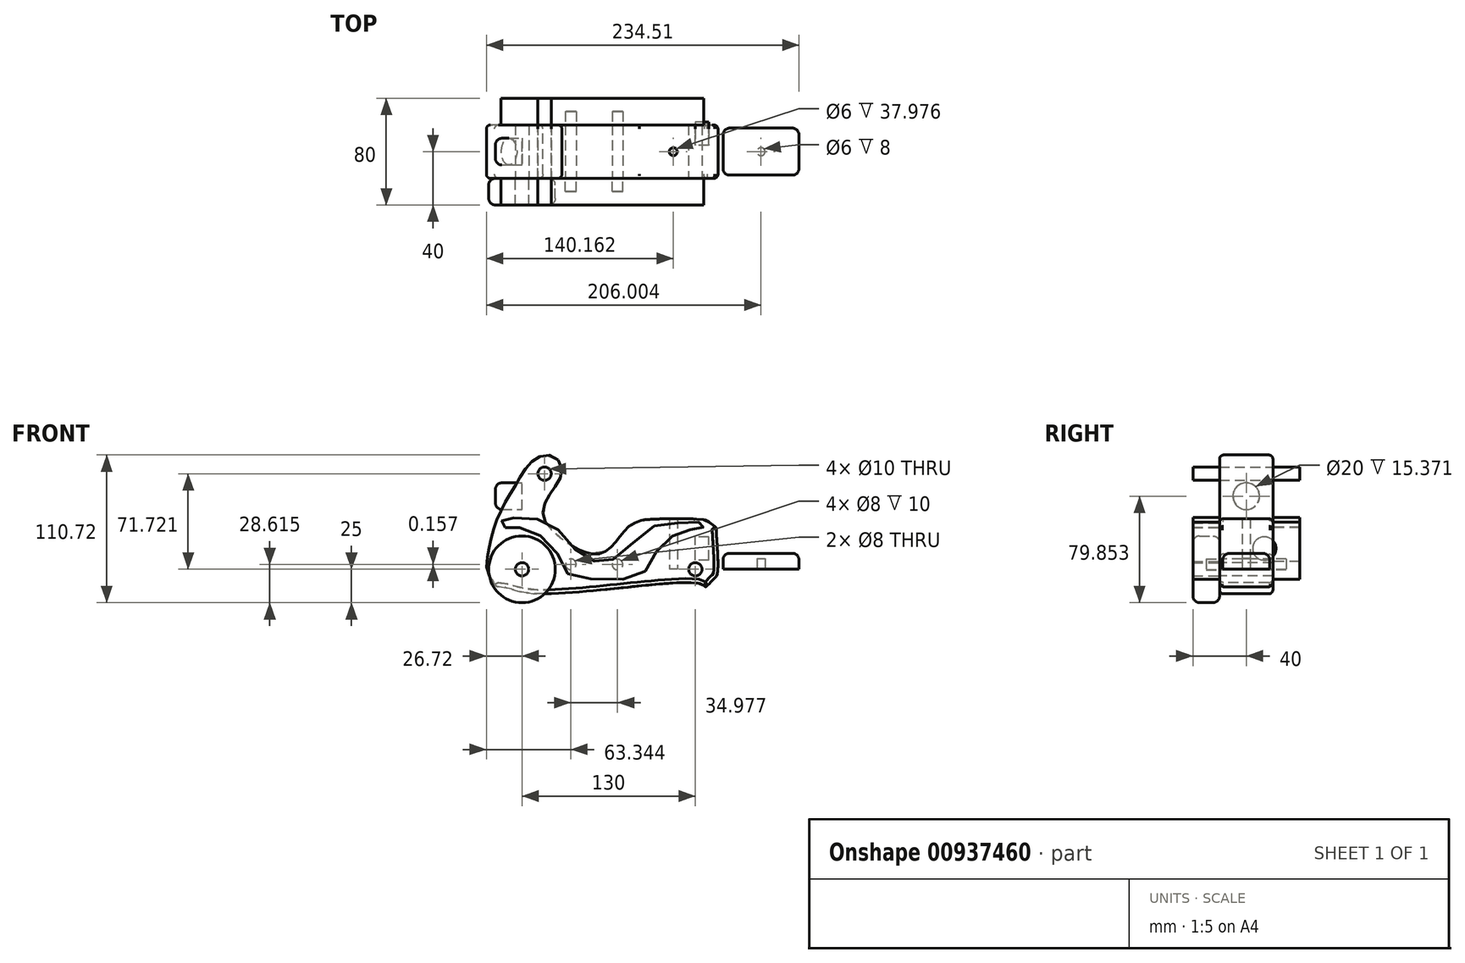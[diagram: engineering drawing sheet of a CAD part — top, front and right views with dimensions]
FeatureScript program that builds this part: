
annotation { "Feature Type Name" : "Feature", "Feature Type Description" : "" }
export const myFeature = defineFeature(function(context is Context, id is Id, definition is map)
    precondition{}
    {
        {
            var Q0;
            Q0=qCreatedBy(makeId("Front.planeOp"),FACE);
            var sketch = newSketch(context, id + "F0", { "sketchPlane" : qUnion([Q0])});
            skCircle(sketch, "E0", {"center": v(0, 0) * mm, "radius": 25 * mm});
            skCircle(sketch, "E1", {"center": v(-130, 0) * mm, "radius": 25 * mm});
            skFitSpline(sketch, "E2", {"points": [v(-142.69, -13.62) * mm, v(3.6, -12.42) * mm, v(8.41, -12.12) * mm, v(12.62, -8.21) * mm, v(15.19, -2.69) * mm, v(15.43, 27.55) * mm, v(14.22, 32.15) * mm, v(11.32, 34.57) * mm, v(6.48, 36.02) * mm, v(-39.96, 36.5) * mm, v(-42.38, 36.02) * mm, v(-48.19, 32.39) * mm, v(-69, 16.67) * mm, v(-87.38, 16.67) * mm, v(-103.82, 27.55) * mm, v(-111.42, 41.65) * mm, v(-106.78, 59.25) * mm, v(-102.15, 74.08) * mm, v(-106.78, 82.42) * mm, v(-117.9, 81.5) * mm, v(-132.73, 65.28) * mm, v(-147.55, 37.02) * mm, v(-154.96, 10.15) * mm, v(-154.9, -3) * mm, v(-152.19, -8.1) * mm, v(-142.69, -13.62) * mm]});
            skSolve(sketch);
        }
        {
            var Q0;
            Q0=qCreatedBy(makeId("Front.planeOp"),FACE);
            var sketch = newSketch(context, id + "F1", { "sketchPlane" : qUnion([Q0])});
            skFitSpline(sketch, "E3.0", {"points": [v(-142.69, -13.62) * mm, v(-117.23, -18.37) * mm, v(4.2, -10.93) * mm, v(7.9, -13.06) * mm, v(13.19, -7.76) * mm, v(16.42, -3.45) * mm, v(15.75, 27.66) * mm, v(14.86, 32.04) * mm, v(10.84, 34.95) * mm, v(7.36, 36.95) * mm, v(-40.36, 36.86) * mm, v(-42.2, 36.14) * mm, v(-49.45, 32.5) * mm, v(-68.05, 13.1) * mm, v(-87.85, 15.1) * mm, v(-104.52, 26.51) * mm, v(-114.25, 41.4) * mm, v(-107.03, 59.23) * mm, v(-100.08, 73.44) * mm, v(-105.87, 84.46) * mm, v(-119.96, 82.96) * mm, v(-133.88, 64.85) * mm, v(-148.53, 37.95) * mm, v(-155.6, 11.4) * mm, v(-155.9, -2.85) * mm, v(-151.67, -8.64) * mm, v(-149.66, -12.32) * mm, v(-142.69, -13.62) * mm]});
            skSolve(sketch);
        }
        {
            var Q0;
            Q0 = qSketchRegion(id + "F1", true);
            extrude(context, id + "F2", {"entities" : qUnion([Q0]), "depth" : 20 * mm, "offsetDistance" : 25 * mm, "hasSecondDirection" : true, "secondDirectionOppositeDirection" : true, "secondDirectionDepth" : 20 * mm});
        }
        {
            var Q0;
            Q0=makeQuery(id+"F2.opExtrude","CAP_FACE",FACE,{"disambiguationData":[OSD([sQuery(id+"F1.wireOp",EDGE,"E3.0")])],"isStart":false});
            var sketch = newSketch(context, id + "F3", { "sketchPlane" : qUnion([Q0])});
            skCircle(sketch, "E4", {"center": v(-113.08, 71.72) * mm, "radius": 5 * mm});
            skCircle(sketch, "E5", {"center": v(-130, 0) * mm, "radius": 5 * mm});
            skCircle(sketch, "E6", {"center": v(0, 0) * mm, "radius": 5 * mm});
            skCircle(sketch, "E7", {"center": v(-93.38, 3.77) * mm, "radius": 4 * mm});
            skCircle(sketch, "E8", {"center": v(-58.4, 3.61) * mm, "radius": 4 * mm});
            skSolve(sketch);
        }
        {
            var Q0;
            Q0 = qSketchRegion(id + "F3", true);
            extrude(context, id + "F4", {"entities" : qUnion([Q0]), "operationType" : NewBodyOperationType.REMOVE, "endBound" : BoundingType.THROUGH_ALL, "oppositeDirection" : true, "depth" : 25 * mm, "offsetDistance" : 25 * mm});
        }
        {
            var Q0;
            Q0=makeQuery(id+"F2.opExtrude","CAP_EDGE",EDGE,{"disambiguationData":[OSD([sQuery(id+"F1.wireOp",EDGE,"E3.0")])],"isStart":false});
            var Q1;
            Q1=makeQuery(id+"F2.opExtrude","CAP_EDGE",EDGE,{"disambiguationData":[OSD([sQuery(id+"F1.wireOp",EDGE,"E3.0")])],"isStart":true});
            fillet(context, id + "F5", {"entities" : qUnion([Q0, Q1]), "radius" : 3 * mm, "tangentPropagation" : true, "allowEdgeOverflow" : false});
        }
        {
            var Q0;
            Q0=makeQuery(id+"F2.opExtrude","CAP_FACE",FACE,{"disambiguationData":[OSD([sQuery(id+"F1.wireOp",EDGE,"E3.0")])],"isStart":false});
            var sketch = newSketch(context, id + "F6", { "sketchPlane" : qUnion([Q0])});
            skFitSpline(sketch, "E9", {"points": [v(-142.57, 31.36) * mm, v(-136.56, 31.66) * mm, v(-122.6, 28.43) * mm, v(-105.17, 15) * mm, v(-95.7, -3.19) * mm, v(-74.3, -7.15) * mm, v(-41.33, -4.69) * mm, v(-32.02, 8.83) * mm, v(-18.8, 23.85) * mm, v(-6.49, 29.25) * mm, v(4.03, 30.46) * mm, v(6.11, 31.78) * mm, v(6.11, 34.02) * mm, v(3.37, 35.44) * mm, v(-10.73, 34.74) * mm, v(-32.01, 31.84) * mm, v(-56.2, 11.04) * mm, v(-65.88, 6.44) * mm, v(-81.93, 8.1) * mm, v(-98.45, 25.17) * mm, v(-115.7, 36.78) * mm, v(-136.43, 38.66) * mm, v(-144.17, 37.2) * mm, v(-145.3, 35.8) * mm, v(-145.64, 32.92) * mm, v(-142.57, 31.36) * mm]});
            skSolve(sketch);
        }
        {
            var Q0;
            Q0 = qSketchRegion(id + "F6", true);
            extrude(context, id + "F7", {"entities" : qUnion([Q0]), "depth" : 20 * mm, "offsetDistance" : 25 * mm});
        }
        {
            var Q0;
            Q0=makeQuery(id+"F7.opExtrude","CAP_FACE",FACE,{"disambiguationData":[OSD([sQuery(id+"F6.wireOp",EDGE,"E9")])],"isStart":true});
            var sketch = newSketch(context, id + "F8", { "sketchPlane" : qUnion([Q0])});
            skCircle(sketch, "E10.0", {"center": v(58.4, 3.61) * mm, "radius": 4 * mm});
            skCircle(sketch, "E11.0", {"center": v(93.38, 3.77) * mm, "radius": 4 * mm});
            skSolve(sketch);
        }
        {
            var Q0;
            Q0 = qSketchRegion(id + "F8", true);
            extrude(context, id + "F9", {"entities" : qUnion([Q0]), "operationType" : NewBodyOperationType.REMOVE, "oppositeDirection" : true, "depth" : 10 * mm, "offsetDistance" : 25 * mm});
        }
        {
            var Q0;
            Q0=qCreatedBy(makeId("Front.planeOp"),FACE);
            var sketch = newSketch(context, id + "F10", { "sketchPlane" : qUnion([Q0])});
            skCircle(sketch, "E12.0", {"center": v(-113.08, 71.72) * mm, "radius": 5 * mm});
            skSolve(sketch);
        }
        {
            var Q0;
            Q0 = qSketchRegion(id + "F10", true);
            extrude(context, id + "F11", {"entities" : qUnion([Q0]), "depth" : 40 * mm, "offsetDistance" : 25 * mm, "hasSecondDirection" : true, "secondDirectionOppositeDirection" : true, "secondDirectionDepth" : 40 * mm});
        }
        {
            var Q0;
            Q0=makeQuery(id+"F2.opExtrude","CAP_FACE",FACE,{"disambiguationData":[OSD([sQuery(id+"F1.wireOp",EDGE,"E3.0")])],"isStart":false});
            var sketch = newSketch(context, id + "F12", { "sketchPlane" : qUnion([Q0])});
            skCircle(sketch, "E13.0", {"center": v(-130, 0) * mm, "radius": 25 * mm});
            skCircle(sketch, "E14.0", {"center": v(-130, 0) * mm, "radius": 5 * mm});
            skSolve(sketch);
        }
        {
            var Q0;
            Q0 = qSketchRegion(id + "F12", true);
            extrude(context, id + "F13", {"entities" : qUnion([Q0]), "depth" : 20 * mm, "offsetDistance" : 25 * mm});
        }
        {
            var Q0;
            Q0=makeQuery(id+"F13.opExtrude","CAP_EDGE",EDGE,{"disambiguationData":[OSD([sQuery(id+"F12.wireOp",EDGE,"E13.0")])],"isStart":false});
            var Q1;
            {var subQ0=sQuery(id+"F12.wireOp",EDGE,"E13.0");Q1=makeQuery(id+"F13.boolean.opBoolean","SPLIT",EDGE,{"disambiguationData":[topologyDisambiguationEdgeConnected([makeQuery(id+"F13.opExtrude","CAP_FACE",FACE,{"disambiguationData":[OSD([subQ0,sQuery(id+"F12.wireOp",EDGE,"E14.0")])],"isStart":true})])],"derivedFrom":makeQuery(id+"F13.opExtrude","CAP_EDGE",EDGE,{"disambiguationData":[OSD([subQ0])],"isStart":true})});}
            fillet(context, id + "F14", {"entities" : qUnion([Q0, Q1]), "radius" : 5 * mm, "tangentPropagation" : true, "allowEdgeOverflow" : false});
        }
        {
            var Q0;
            Q0=makeQuery(id+"F7.opExtrude","SWEPT_BODY",BODY,{"disambiguationData":[OSD([sQuery(id+"F6.wireOp",EDGE,"E9")])]});
            var Q1;
            Q1=qCreatedBy(makeId("Front.planeOp"),FACE);
            mirror(context, id + "F15", {"entities" : qUnion([Q0]), "mirrorPlane" : qUnion([Q1])});
        }
        {
            var Q0;
            Q0=qCreatedBy(makeId("Right.planeOp"),FACE);
            cPlane(context, id + "F16", {"entities" : qUnion([Q0]), "cplaneType" : CPlaneType.OFFSET, "offset" : 130 * mm, "oppositeDirection" : true, "width" : 150 * mm, "height" : 150 * mm});
        }
        {
            var Q0;
            Q0=qCreatedBy(id+"F16.planeOp",FACE);
            var sketch = newSketch(context, id + "F17", { "sketchPlane" : qUnion([Q0])});
            skCircle(sketch, "E15", {"center": v(0, 54.85) * mm, "radius": 10 * mm});
            skSolve(sketch);
        }
        {
            var Q0;
            Q0 = qSketchRegion(id + "F17", true);
            extrude(context, id + "F18", {"entities" : qUnion([Q0]), "operationType" : NewBodyOperationType.REMOVE, "oppositeDirection" : true, "depth" : 20 * mm, "offsetDistance" : 25 * mm});
        }
        {
            var Q0;
            Q0=makeQuery(id+"F18.boolean.opBoolean","COPY",FACE,{"derivedFrom":makeQuery(id+"F18.opExtrude","CAP_FACE",FACE,{"disambiguationData":[OSD([sQuery(id+"F17.wireOp",EDGE,"E15")])],"isStart":true})});
            var sketch = newSketch(context, id + "F19", { "sketchPlane" : qUnion([Q0])});
            skCircle(sketch, "E16.0", {"center": v(0, 54.85) * mm, "radius": 10 * mm});
            skSolve(sketch);
        }
        {
            var Q0;
            Q0 = qSketchRegion(id + "F19", true);
            extrude(context, id + "F20", {"entities" : qUnion([Q0]), "depth" : 20 * mm, "offsetDistance" : 25 * mm});
        }
        {
            var Q0;
            Q0=makeQuery(id+"F20.opExtrude","CAP_EDGE",EDGE,{"disambiguationData":[OSD([sQuery(id+"F19.wireOp",EDGE,"E16.0")])],"isStart":false});
            fillet(context, id + "F21", {"entities" : qUnion([Q0]), "radius" : 5 * mm, "tangentPropagation" : true, "allowEdgeOverflow" : false});
        }
        {
            var Q0;
            Q0=qCreatedBy(makeId("Top.planeOp"),FACE);
            var sketch = newSketch(context, id + "F22", { "sketchPlane" : qUnion([Q0])});
            skLineSegment(sketch, "E17.bottom", {"start": v(77.8, 17.62) * mm, "end": v(20.78, 17.62) * mm});
            skLineSegment(sketch, "E17.top", {"start": v(77.8, -17.62) * mm, "end": v(20.78, -17.62) * mm});
            skLineSegment(sketch, "E17.left", {"start": v(77.8, 17.62) * mm, "end": v(77.8, -17.62) * mm});
            skLineSegment(sketch, "E17.right", {"start": v(20.78, 17.62) * mm, "end": v(20.78, -17.62) * mm});
            skPoint(sketch, "E17.middle", {"position": v(49.28, 0) * mm});
            skSolve(sketch);
        }
        {
            var Q0;
            Q0 = qSketchRegion(id + "F22", true);
            extrude(context, id + "F23", {"entities" : qUnion([Q0]), "depth" : 12 * mm, "offsetDistance" : 25 * mm});
        }
        {
            var Q0;
            Q0=makeQuery(id+"F23.opExtrude","SWEPT_EDGE",EDGE,{"disambiguationData":[OSD([sQuery(id+"F22.wireOp",EDGE,"E17.bottom"),sQuery(id+"F22.wireOp",EDGE,"E17.left")])]});
            var Q1;
            Q1=makeQuery(id+"F23.opExtrude","SWEPT_EDGE",EDGE,{"disambiguationData":[OSD([sQuery(id+"F22.wireOp",EDGE,"E17.top"),sQuery(id+"F22.wireOp",EDGE,"E17.left")])]});
            var Q2;
            Q2=makeQuery(id+"F23.opExtrude","SWEPT_EDGE",EDGE,{"disambiguationData":[OSD([sQuery(id+"F22.wireOp",EDGE,"E17.top"),sQuery(id+"F22.wireOp",EDGE,"E17.right")])]});
            var Q3;
            Q3=makeQuery(id+"F23.opExtrude","SWEPT_EDGE",EDGE,{"disambiguationData":[OSD([sQuery(id+"F22.wireOp",EDGE,"E17.bottom"),sQuery(id+"F22.wireOp",EDGE,"E17.right")])]});
            var Q4;
            Q4=makeQuery(id+"F23.opExtrude","CAP_FACE",FACE,{"disambiguationData":[OSD([sQuery(id+"F22.wireOp",EDGE,"E17.bottom"),sQuery(id+"F22.wireOp",EDGE,"E17.top"),sQuery(id+"F22.wireOp",EDGE,"E17.left"),sQuery(id+"F22.wireOp",EDGE,"E17.right")])],"isStart":false});
            fillet(context, id + "F24", {"entities" : qUnion([Q0, Q1, Q2, Q3, Q4]), "radius" : 5 * mm, "tangentPropagation" : true, "allowEdgeOverflow" : false});
        }
        {
            var Q0;
            Q0=qCreatedBy(makeId("Top.planeOp"),FACE);
            var sketch = newSketch(context, id + "F25", { "sketchPlane" : qUnion([Q0])});
            skCircle(sketch, "E18", {"center": v(-16.56, 0) * mm, "radius": 3 * mm});
            skSolve(sketch);
        }
        {
            var Q0;
            Q0 = qSketchRegion(id + "F25", true);
            extrude(context, id + "F26", {"entities" : qUnion([Q0]), "operationType" : NewBodyOperationType.REMOVE, "endBound" : BoundingType.THROUGH_ALL, "depth" : 25 * mm, "offsetDistance" : 25 * mm});
        }
        {
            var Q0;
            Q0=makeQuery(id+"F23.opExtrude","CAP_FACE",FACE,{"disambiguationData":[OSD([sQuery(id+"F22.wireOp",EDGE,"E17.bottom"),sQuery(id+"F22.wireOp",EDGE,"E17.top"),sQuery(id+"F22.wireOp",EDGE,"E17.left"),sQuery(id+"F22.wireOp",EDGE,"E17.right")])],"isStart":true});
            var sketch = newSketch(context, id + "F27", { "sketchPlane" : qUnion([Q0])});
            skLineSegment(sketch, "E19", {"start": v(25.78, -12.62) * mm, "end": v(72.8, 12.62) * mm, "construction": true});
            skCircle(sketch, "E20", {"center": v(49.28, 0) * mm, "radius": 3 * mm});
            skSolve(sketch);
        }
        {
            var Q0;
            Q0 = qSketchRegion(id + "F27", true);
            extrude(context, id + "F28", {"entities" : qUnion([Q0]), "operationType" : NewBodyOperationType.REMOVE, "oppositeDirection" : true, "depth" : 8 * mm, "offsetDistance" : 25 * mm});
        }
        {
            var Q0;
            Q0=qCreatedBy(makeId("Right.planeOp"),FACE);
            var sketch = newSketch(context, id + "F29", { "sketchPlane" : qUnion([Q0])});
            skCircle(sketch, "E21", {"center": v(13.58, 15.56) * mm, "radius": 8.77 * mm});
            skSolve(sketch);
        }
        {
            var Q0;
            Q0 = qSketchRegion(id + "F29", true);
            extrude(context, id + "F30", {"entities" : qUnion([Q0]), "depth" : 10 * mm, "offsetDistance" : 25 * mm});
        }
    });
